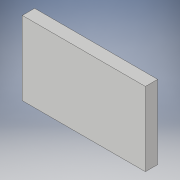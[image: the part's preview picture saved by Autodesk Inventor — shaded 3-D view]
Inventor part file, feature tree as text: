
AUTODESK INVENTOR PART (.ipt)
format: ipt  version: 2017 (Build 210142000, 142)  size: 85,504 bytes
history: native  units: in
note: dims shown in document units (in); Inventor stores cm internally (conversion verified against a paired STEP export)
features: extrude x1, sketch x1
ambient origin geometry x8: Origin, YZ Plane, XZ Plane, XY Plane, X Axis, Y Axis, Z Axis, Center Point
bodies: Solid1 (feature_tree)
feature tree (2):
  extrude  "Extrusion1"  Depth=1.5in
  sketch  "Sketch1"  dims[d0=2.5in d1=1.5in d2=0.25in d3=0.0in]
